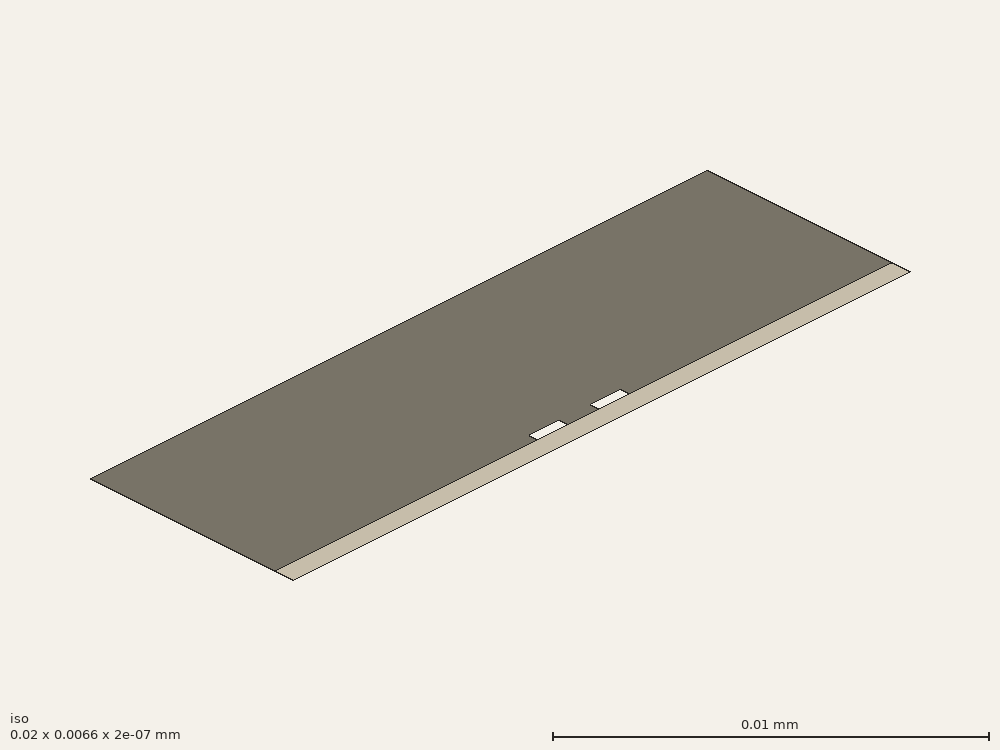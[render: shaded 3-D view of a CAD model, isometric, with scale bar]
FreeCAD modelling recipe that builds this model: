
FCSTD DOCUMENT  (FreeCAD 0.19R)
Label: diffPair
License: All rights reserved
LicenseURL: http://en.wikipedia.org/wiki/All_rights_reserved
objects: Part::Part2DObjectPython×6, App::FeaturePython×4, Part::FeaturePython×2
note: 8 computed .brp shape members not serialized (recipe doc carries the construction recipe); baked Part::Feature solids carry a one-line shape summary decoded from their .brp

FEATURE [Part::Part2DObjectPython] Rectangle  label="substrate"  # Draft 2D object (typed FeaturePython)
  Area = 12.7
  ChamferSize = 0
  Columns = 1
  FilletRadius = 0
  Height = 0.635
  Length = 20
  MakeFace = true
  Placement = pos=(-10,0,0) rot=(0,0,1;0rad)
  Rows = 1
FEATURE [Part::Part2DObjectPython] Wire  label="air"  # Draft 2D object (typed FeaturePython)
  Area = 119.4
  ChamferSize = 0
  Closed = true
  End = (-1.5,0.635,0)
  FilletRadius = 0
  Length = 53.2
  MakeFace = true
  Placement = pos=(-10,0.635,0) rot=(0,0,1;0rad)
  Points = (12) [(0,0,0),(0,6,0),(20,6,0),(20,-6.66134e-16,0),(11.5,-3.33067e-16,0),(11.5,0.3,0),(10.5,0.3,0),(10.5,-3.33067e-16,0),(9.5,-3.33067e-16,0),(9.5,0.3,0),(8.5,0.3,0),(8.5,-3.33067e-16,0)]
  Start = (-10,0.635,0)
  Subdivisions = 0
FEATURE [Part::FeaturePython] BooleanFragments  # WARN: FeaturePython — macro-defined, semantics opaque (R4)
  Mode = 0
  Objects = -> [Rectangle,Wire]
  Tolerance = 0
FEATURE [Part::FeaturePython] Clone  label="scaled to mm"  # Draft clone (typed FeaturePython)
  AttacherType = Attacher::AttachEngine3D
  Fuse = false
  Objects = -> [BooleanFragments]
  Scale = (0.001,0.001,1)
FEATURE [Part::Part2DObjectPython] Line  label="_PV1"  # Draft 2D object (typed FeaturePython)
  Area = 0
  ChamferSize = 0
  Closed = false
  End = (-0.001,0,0)
  FilletRadius = 0
  Length = 0.000635
  MakeFace = false
  Placement = pos=(-0.003,0.000635,0) rot=(0,0,1;0rad)
  Points = (2) [(0.002,0,0),(0.002,-0.000635,0)]
  Start = (-0.001,0.000635,0)
  Subdivisions = 0
FEATURE [Part::Part2DObjectPython] Line001  label="_PV2"  # Draft 2D object (typed FeaturePython)
  Area = 0
  ChamferSize = 0
  Closed = false
  End = (0.001,0,0)
  FilletRadius = 0
  Length = 0.000635
  MakeFace = true
  Placement = pos=(0.001,0.000635,0) rot=(0,0,1;0rad)
  Points = (2) [(0,0,0),(0,-0.000635,0)]
  Start = (0.001,0.000635,0)
  Subdivisions = 0
FEATURE [Part::Part2DObjectPython] Rectangle003  label="_Pline1"  # Draft 2D object (typed FeaturePython)
  Area = 0
  ChamferSize = 0
  Columns = 1
  FilletRadius = 0
  Height = 0.0003
  Length = 0.001
  MakeFace = false
  Placement = pos=(-0.0015,0.000635,0) rot=(0,0,1;0rad)
  Rows = 1
FEATURE [Part::Part2DObjectPython] Rectangle002  label="_Pline2"  # Draft 2D object (typed FeaturePython)
  Area = 0
  ChamferSize = 0
  Columns = 1
  FilletRadius = 0
  Height = 0.0003
  Length = 0.001
  MakeFace = false
  Placement = pos=(0.0005,0.000635,0) rot=(0,0,1;0rad)
  Rows = 1
FEATURE [App::FeaturePython] Text  label="_M1(current){line1,line2}"  # WARN: FeaturePython — macro-defined, semantics opaque (R4)
  Placement = pos=(-0.00185272,-0.00154398,0) rot=(0,0,1;0rad)
  Text = .
FEATURE [App::FeaturePython] Text001  label="_M1(voltage){V1}"  # WARN: FeaturePython — macro-defined, semantics opaque (R4)
  Placement = pos=(-0.00185272,-0.00154398,0) rot=(0,0,1;0rad)
  Text = .
FEATURE [App::FeaturePython] Text002  label="_M2(current){line1}"  # WARN: FeaturePython — macro-defined, semantics opaque (R4)
  Placement = pos=(-0.00185272,-0.00154398,0) rot=(0,0,1;0rad)
  Text = .
FEATURE [App::FeaturePython] Text003  label="_M2(voltage){V1,-V2}"  # WARN: FeaturePython — macro-defined, semantics opaque (R4)
  Placement = pos=(-0.00185272,-0.00154398,0) rot=(0,0,1;0rad)
  Text = .
